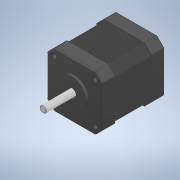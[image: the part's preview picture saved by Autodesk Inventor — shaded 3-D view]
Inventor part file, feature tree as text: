
AUTODESK INVENTOR PART (.ipt)
format: ipt  version: 2022 (Build 260153000, 153)  size: 725,504 bytes
history: imported  units: in
note: dims shown in document units (in); Inventor stores cm internally (conversion verified against a paired STEP export)
features: sketch x4, imported_body x1
ambient origin geometry x8: Origin, YZ Plane, XZ Plane, XY Plane, X Axis, Y Axis, Z Axis, Center Point
bodies: Solid1 (imported_parasolid), Body1 (imported_parasolid)
feature tree (5):
  sketch  "Sketch1"
  sketch  "Sketch2"
  sketch  "Sketch3"
  sketch  "Sketch4"
  imported_body  NMx_Import_Brep_tag  [imported B-rep: ~13 faces, bbox_mm=[3.7, 9.8, 0.0]]
